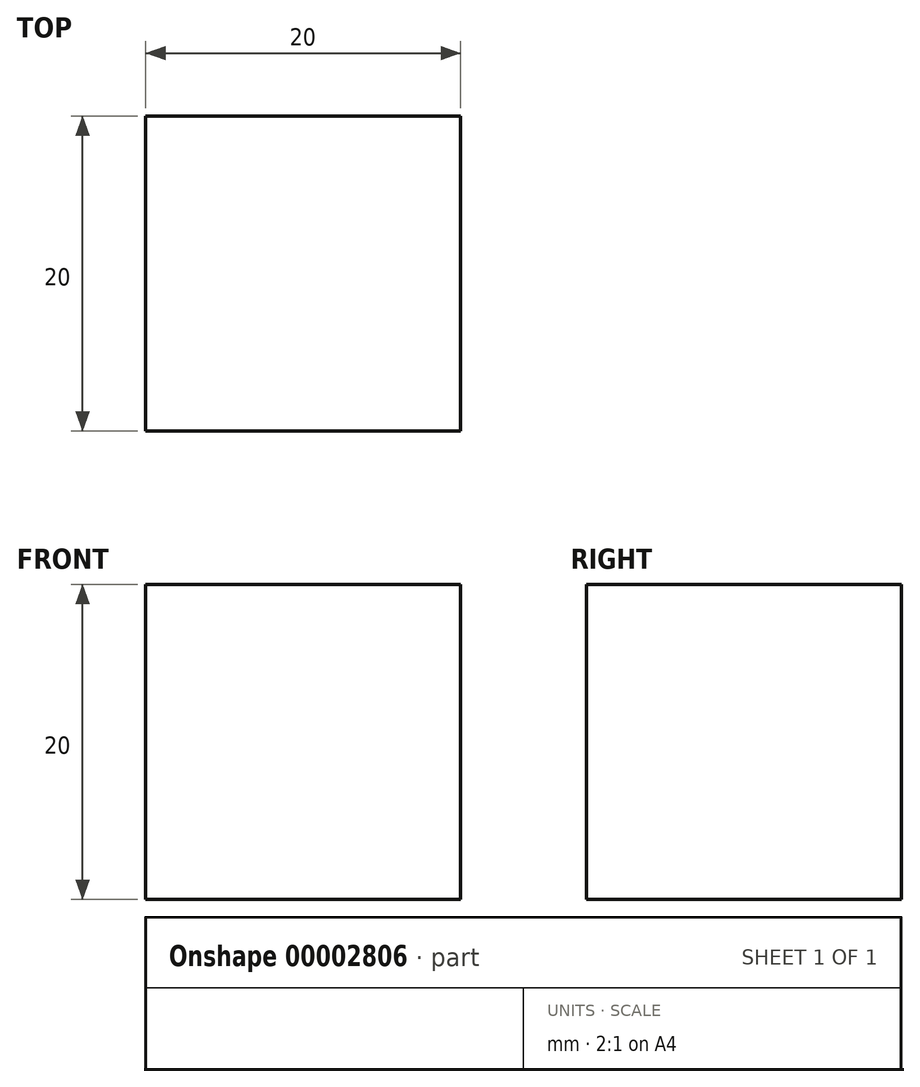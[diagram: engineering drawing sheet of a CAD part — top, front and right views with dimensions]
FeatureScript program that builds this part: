
annotation { "Feature Type Name" : "Feature", "Feature Type Description" : "" }
export const myFeature = defineFeature(function(context is Context, id is Id, definition is map)
    precondition{}
    {
        {
            var Q0;
            Q0=qCreatedBy(makeId("Front.planeOp"),FACE);
            var sketch = newSketch(context, id + "F0", { "sketchPlane" : qUnion([Q0])});
            skLineSegment(sketch, "E0.bottom", {"start": v(-65.68, 63.48) * mm, "end": v(-45.68, 63.48) * mm});
            skLineSegment(sketch, "E0.top", {"start": v(-65.68, 43.48) * mm, "end": v(-45.68, 43.48) * mm});
            skLineSegment(sketch, "E0.left", {"start": v(-65.68, 63.48) * mm, "end": v(-65.68, 43.48) * mm});
            skLineSegment(sketch, "E0.right", {"start": v(-45.68, 63.48) * mm, "end": v(-45.68, 43.48) * mm});
            skSolve(sketch);
        }
        {
            var Q0;
            Q0 = qSketchRegion(id + "F0", true);
            extrude(context, id + "F1", {"entities" : qUnion([Q0]), "depth" : 20 * mm});
        }
    });
